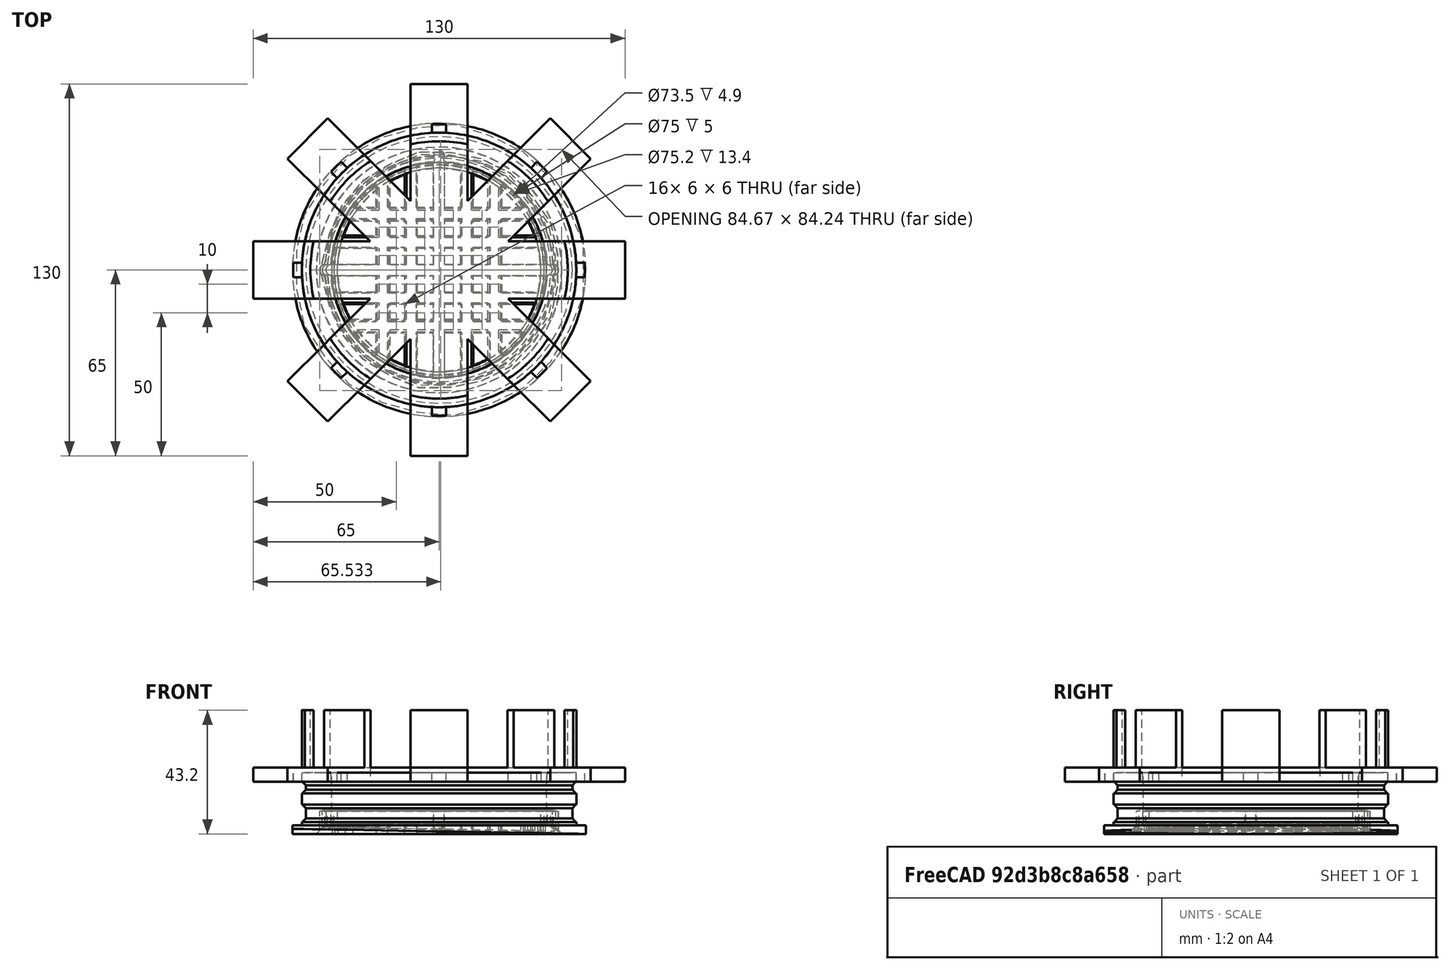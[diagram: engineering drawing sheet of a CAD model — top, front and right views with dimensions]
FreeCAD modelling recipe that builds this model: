
FCSTD DOCUMENT  (FreeCAD 0.18R4 (GitTag))
Label: rejilla_banio
License: CreativeCommons Attribution-ShareAlike
LicenseURL: http://creativecommons.org/licenses/by-sa/4.0/
objects: Part::Cylinder×56, Part::Cut×50, Part::Box×40, Part::MultiFuse×22, Part::FeaturePython×9, Part::Cone×3, Part::Plane×3, Part::Chamfer×2, App::DocumentObjectGroup×2, Part::Feature×2
note: 187 computed .brp shape members not serialized (recipe doc carries the construction recipe); baked Part::Feature solids carry a one-line shape summary decoded from their .brp

FEATURE [Part::Cone] Cone
  Angle = 360
  AttacherType = Attacher::AttachEngine3D
  Height = 5
  Placement = pos=(0,0,-15.2) rot=(0,1,0;3.14159rad)
  Radius1 = 40
  Radius2 = 45
FEATURE [Part::Cylinder] Cylinder007
  Angle = 360
  AttacherType = Attacher::AttachEngine3D
  Height = 25
  Placement = pos=(0,0,-23) rot=(0,0,1;0rad)
  Radius = 45
FEATURE [Part::Cylinder] Cylinder006  label="ajustar_radio_de_este"
  Angle = 360
  AttacherType = Attacher::AttachEngine3D
  Height = 5
  Placement = pos=(0,0,-20.2) rot=(0,0,1;0rad)
  Radius = 51.3
FEATURE [Part::Cut] Cut001
  Base = -> Cylinder006
  Tool = -> Cylinder007
FEATURE [Part::Cylinder] Cylinder001
  Angle = 360
  AttacherType = Attacher::AttachEngine3D
  Height = 4
  Placement = pos=(0,0,-4) rot=(0,0,1;0rad)
  Radius = 46.6
FEATURE [Part::Cylinder] Cylinder002
  Angle = 360
  AttacherType = Attacher::AttachEngine3D
  Height = 4
  Placement = pos=(0,0,-8) rot=(0,0,1;0rad)
  Radius = 48
FEATURE [Part::Cylinder] Cylinder003
  Angle = 360
  AttacherType = Attacher::AttachEngine3D
  Height = 6
  Placement = pos=(0,0,-14) rot=(0,0,1;0rad)
  Radius = 46.6
FEATURE [Part::Cylinder] Cylinder005
  Angle = 360
  AttacherType = Attacher::AttachEngine3D
  Height = 25
  Placement = pos=(0,0,-18) rot=(0,0,1;0rad)
  Radius = 45
FEATURE [Part::Cylinder] Cylinder008
  Angle = 360
  AttacherType = Attacher::AttachEngine3D
  Height = 23.4
  Placement = pos=(0,0,-20.2) rot=(0,0,1;0rad)
  Radius = 45
FEATURE [Part::Cylinder] Cylinder009
  Angle = 360
  AttacherType = Attacher::AttachEngine3D
  Height = 27.4
  Placement = pos=(0,0,-17) rot=(0,0,1;0rad)
  Radius = 40
FEATURE [Part::MultiFuse] Fusion002
  Shapes = -> [Cylinder009,Cone]
FEATURE [Part::Cut] Cut002
  Base = -> Cylinder008
  Tool = -> Fusion002
FEATURE [Part::Cylinder] Cylinder019  label="ajustar_radio_de_este001"
  Angle = 360
  AttacherType = Attacher::AttachEngine3D
  Height = 5
  Placement = pos=(0,0,-23.2) rot=(0,0,1;0rad)
  Radius = 68.3
FEATURE [Part::Cylinder] Cylinder
  Angle = 360
  AttacherType = Attacher::AttachEngine3D
  Height = 3.2
  Radius = 48
FEATURE [Part::Cylinder] Cylinder004
  Angle = 360
  AttacherType = Attacher::AttachEngine3D
  Height = 1.2
  Placement = pos=(0,0,-15.2) rot=(0,0,1;0rad)
  Radius = 48
FEATURE [Part::MultiFuse] Fusion
  Shapes = -> [Cylinder004,Cylinder,Cylinder003,Cylinder001,Cylinder002]
FEATURE [Part::Cut] Cut
  Base = -> Fusion
  Tool = -> Cylinder005
FEATURE [Part::MultiFuse] Fusion001
  Shapes = -> [Cut001,Cut]
FEATURE [Part::MultiFuse] Fusion003  label="rejilla_sin_cortar_oblicuo_sin_chaflan"
  Shapes = -> [Fusion001,Cut002]
FEATURE [Part::Chamfer] Chamfer
  Base = -> Fusion003
  Edges = 2 edges r=1.2: [Edge12,Edge24]
FEATURE [Part::Chamfer] Chamfer001  label="rejilla__exteriorsin_cortar_oblicuo_alta"
  Base = -> Chamfer
  Edges = 2 edges r=1.2: [Edge8,Edge26]
FEATURE [Part::Cut] Cut009  label="rejilla__exterior_sin_cortar_oblicuo_sin_muescas_01"
  Base = -> Chamfer001
  Tool = -> Cylinder019
FEATURE [Part::Cylinder] Cylinder057
  Angle = 360
  AttacherType = Attacher::AttachEngine3D
  Height = 7.8
  Placement = pos=(39.8,0,-18) rot=(0,0,1;0rad)
  Radius = 2
FEATURE [Part::Cylinder] Cylinder054
  Angle = 360
  AttacherType = Attacher::AttachEngine3D
  Height = 7.8
  Placement = pos=(0,39.8,-18) rot=(0,0,1;0rad)
  Radius = 2
FEATURE [Part::Cylinder] Cylinder058
  Angle = 360
  AttacherType = Attacher::AttachEngine3D
  Height = 7.8
  Placement = pos=(-39.8,0,-18) rot=(0,0,1;0rad)
  Radius = 2
FEATURE [Part::Cylinder] Cylinder055
  Angle = 360
  AttacherType = Attacher::AttachEngine3D
  Height = 13.4
  Placement = pos=(0,0,-10.2) rot=(0,0,1;0rad)
  Radius = 40
FEATURE [Part::Cylinder] Cylinder056
  Angle = 360
  AttacherType = Attacher::AttachEngine3D
  Height = 13.4
  Placement = pos=(0,0,-10.2) rot=(0,0,1;0rad)
  Radius = 37.6
FEATURE [Part::Cut] Cut026
  Base = -> Cylinder055
  Tool = -> Cylinder056
FEATURE [Part::MultiFuse] Fusion019  label="rejilla__exterior_sin_cortar_oblicuo_sin_muescas"
  Shapes = -> [Cut009,Cut026]
FEATURE [Part::Cut] Cut027
  Base = -> Fusion019
  Tool = -> Cylinder054
FEATURE [Part::Cut] Cut028
  Base = -> Cut027
  Tool = -> Cylinder057
FEATURE [Part::Cut] Cut029  label="rejilla__exterior_sin_cortar"
  Base = -> Cut028
  Tool = -> Cylinder058
FEATURE [Part::Cone] Cone003
  Angle = 360
  AttacherType = Attacher::AttachEngine3D
  Height = 5
  Placement = pos=(0,0,-15.2) rot=(0,1,0;3.14159rad)
  Radius1 = 39.85
  Radius2 = 44.9
FEATURE [Part::Box] Box015  label="Cube015"
  AttacherType = Attacher::AttachEngine3D
  Height = 5
  Length = 74
  Placement = pos=(-8,-37,-41) rot=(0,0,1;1.5708rad)
  Width = 4
FEATURE [Part::Cylinder] Cylinder046
  Angle = 360
  AttacherType = Attacher::AttachEngine3D
  Height = 5
  Placement = pos=(0,0,-41) rot=(0,0,1;0rad)
  Radius = 45
FEATURE [Part::Cylinder] Cylinder048
  Angle = 360
  AttacherType = Attacher::AttachEngine3D
  Height = 5
  Placement = pos=(0,0,-41) rot=(0,0,1;0rad)
  Radius = 37.5
FEATURE [Part::Box] Box016  label="Cube016"
  AttacherType = Attacher::AttachEngine3D
  Height = 5
  Length = 74
  Placement = pos=(-37,8,-41) rot=(0,0,1;0rad)
  Width = 4
FEATURE [Part::Box] Box017  label="Cube017"
  AttacherType = Attacher::AttachEngine3D
  Height = 5
  Length = 66
  Placement = pos=(-33,18,-41) rot=(0,0,1;0rad)
  Width = 4
FEATURE [Part::Cylinder] Cylinder042
  Angle = 360
  AttacherType = Attacher::AttachEngine3D
  Height = 5
  Radius = 37.5
FEATURE [Part::Cylinder] Cylinder043
  Angle = 360
  AttacherType = Attacher::AttachEngine3D
  Height = 5
  Radius = 39.9
FEATURE [Part::Cut] Cut021
  Base = -> Cylinder043
  Placement = pos=(0,0,-15.2) rot=(0,0,1;0rad)
  Tool = -> Cylinder042
FEATURE [Part::Box] Box010  label="Cube010"
  AttacherType = Attacher::AttachEngine3D
  Height = 5
  Length = 74
  Placement = pos=(12,-37,-41) rot=(0,0,1;1.5708rad)
  Width = 4
FEATURE [Part::Cylinder] Cylinder045
  Angle = 360
  AttacherType = Attacher::AttachEngine3D
  Height = 7.8
  Placement = pos=(-39.8,0,-18) rot=(0,0,1;0rad)
  Radius = 1.9
FEATURE [Part::Box] Box012  label="Cube012"
  AttacherType = Attacher::AttachEngine3D
  Height = 5
  Length = 66
  Placement = pos=(22,-33,-41) rot=(0,0,1;1.5708rad)
  Width = 4
FEATURE [Part::Cylinder] Cylinder047
  Angle = 360
  AttacherType = Attacher::AttachEngine3D
  Height = 7.8
  Placement = pos=(39.8,0,-18) rot=(0,0,1;0rad)
  Radius = 1.9
FEATURE [Part::Cylinder] Cylinder044
  Angle = 360
  AttacherType = Attacher::AttachEngine3D
  Height = 10
  Placement = pos=(0,0,-49) rot=(0,0,1;0rad)
  Radius = 50
FEATURE [Part::Box] Box013  label="Cube013"
  AttacherType = Attacher::AttachEngine3D
  Height = 5
  Length = 66
  Placement = pos=(-18,-33,-41) rot=(0,0,1;1.5708rad)
  Width = 4
FEATURE [Part::Box] Box014  label="Cube014"
  AttacherType = Attacher::AttachEngine3D
  Height = 5
  Length = 76
  Placement = pos=(-38,-2,-41) rot=(0,0,1;0rad)
  Width = 4
FEATURE [Part::Box] Box011  label="Cube011"
  AttacherType = Attacher::AttachEngine3D
  Height = 5
  Length = 66
  Placement = pos=(-33,-22,-41) rot=(0,0,1;0rad)
  Width = 4
FEATURE [Part::Cylinder] Cylinder050  label="ajustar_radio_de_este005"
  Angle = 360
  AttacherType = Attacher::AttachEngine3D
  Height = 5
  Placement = pos=(0,0,-23.2) rot=(0,0,1;0rad)
  Radius = 68.3
FEATURE [Part::Box] Box019  label="Cube019"
  AttacherType = Attacher::AttachEngine3D
  Height = 5
  Length = 76
  Placement = pos=(2,-38,-41) rot=(0,0,1;1.5708rad)
  Width = 4
FEATURE [Part::Cylinder] Cylinder052
  Angle = 360
  AttacherType = Attacher::AttachEngine3D
  Height = 5
  Placement = pos=(0,0,-41) rot=(0,0,1;0rad)
  Radius = 37.3
FEATURE [Part::Cut] Cut022  label="anillo001"
  Base = -> Cylinder048
  Tool = -> Cylinder052
FEATURE [Part::Cylinder] Cylinder051
  Angle = 360
  AttacherType = Attacher::AttachEngine3D
  Height = 32
  Placement = pos=(0,0,-39) rot=(0,0,1;0rad)
  Radius = 37.5
FEATURE [Part::Cut] Cut019
  Base = -> Cone003
  Tool = -> Cylinder051
FEATURE [Part::MultiFuse] Fusion015  label="rejilla_interior_sin_cortar_oblicuo_sin_tapa_006"
  Shapes = -> [Cut021,Cut019]
FEATURE [Part::Cut] Cut025
  Base = -> Fusion015
  Tool = -> Cylinder050
FEATURE [Part::Cylinder] Cylinder049
  Angle = 360
  AttacherType = Attacher::AttachEngine3D
  Height = 5
  Placement = pos=(0,0,-41) rot=(0,0,1;0rad)
  Radius = 37.5
FEATURE [Part::Cut] Cut020
  Base = -> Cylinder046
  Tool = -> Cylinder049
FEATURE [Part::Cylinder] Cylinder053
  Angle = 360
  AttacherType = Attacher::AttachEngine3D
  Height = 7.8
  Placement = pos=(0,39.8,-18) rot=(0,0,1;0rad)
  Radius = 1.9
FEATURE [Part::Box] Box018  label="Cube018"
  AttacherType = Attacher::AttachEngine3D
  Height = 5
  Length = 74
  Placement = pos=(-37,-12,-41) rot=(0,0,1;0rad)
  Width = 4
FEATURE [Part::MultiFuse] Fusion016
  Shapes = -> [Cut022,Box013,Box012,Box015,Box016,Box018,Box011,Box014,Box017,Box019,Box010]
FEATURE [Part::Cut] Cut023
  Base = -> Fusion016
  Tool = -> Cut020
FEATURE [Part::Cut] Cut024
  Base = -> Cut023
  Placement = pos=(0,0,20.8) rot=(0,0,1;0rad)
  Tool = -> Cylinder044
FEATURE [Part::MultiFuse] Fusion017  label="rejilla__interior_sin_cortar_oblicuo_sin_muescas001"
  Shapes = -> [Cut024,Cut025]
FEATURE [Part::MultiFuse] Fusion014  label="rejilla__interior_sin_cortar_oblicuo001"
  Shapes = -> [Fusion017,Cylinder045,Cylinder047]
FEATURE [Part::MultiFuse] Fusion018  label="rejilla__interior_v2.0_cono_39.85"
  Shapes = -> [Fusion014,Cylinder053]
FEATURE [Part::Plane] Plane
  AttacherType = Attacher::AttachEngine3D
  Length = 300
  Placement = pos=(-150,-150,-14.7) rot=(0,1,0;0.017453rad)
  Width = 300
FEATURE [Part::Plane] Plane001
  AttacherType = Attacher::AttachEngine3D
  Length = 300
  Placement = pos=(-150,-150,-14.7) rot=(0,1,0;0.017453rad)
  Width = 300
FEATURE [Part::FeaturePython] Slice  # WARN: FeaturePython — macro-defined, semantics opaque (R4)
  Base = -> Cut029
  Mode = 1
  Tolerance = 0
  Tools = -> [Plane001]
FEATURE [Part::FeaturePython] Slice_child0  label="rejilla_exterior"  # WARN: FeaturePython — macro-defined, semantics opaque (R4)
  Base = -> Slice
  FilterType = 1
  Invert = false
  OverrideMaxVal = 0
  WindowFrom = 80
  WindowTo = 100
  items = 0
FEATURE [Part::FeaturePython] Slice_child1  label="Slice.1"  # WARN: FeaturePython — macro-defined, semantics opaque (R4)
  Base = -> Slice
  FilterType = 1
  Invert = false
  OverrideMaxVal = 0
  WindowFrom = 80
  WindowTo = 100
  items = 1
FEATURE [App::DocumentObjectGroup] GrExplode_Slice  label="Exploded Slice"
  Group = -> [Slice_child0,Slice_child1]
FEATURE [Part::FeaturePython] Slice001  # WARN: FeaturePython — macro-defined, semantics opaque (R4)
  Base = -> Fusion018
  Mode = 1
  Tolerance = 0
  Tools = -> [Plane]
FEATURE [Part::FeaturePython] Slice001_child0  label="rejilla__interior"  # WARN: FeaturePython — macro-defined, semantics opaque (R4)
  Base = -> Slice001
  FilterType = 1
  Invert = false
  OverrideMaxVal = 0
  WindowFrom = 80
  WindowTo = 100
  items = 0
FEATURE [Part::FeaturePython] Slice001_child1  label="Slice001.1"  # WARN: FeaturePython — macro-defined, semantics opaque (R4)
  Base = -> Slice001
  FilterType = 1
  Invert = false
  OverrideMaxVal = 0
  WindowFrom = 80
  WindowTo = 100
  items = 1
FEATURE [App::DocumentObjectGroup] GrExplode_Slice001  label="Exploded Slice001"
  Group = -> [Slice001_child0,Slice001_child1]
FEATURE [Part::Feature] Slice001_child0001  label="rejilla__interior001"
  shape: bbox 85.47 x 85.49 x 7.864 mm, 285 faces (baked)
FEATURE [Part::Feature] Slice001_child  label="rejilla__interior_095"
  shape: bbox 151.1 x 139.8 x 7.471 mm, 285 faces (baked)
FEATURE [Part::Cylinder] Cylinder059
  Angle = 360
  AttacherType = Attacher::AttachEngine3D
  Height = 5
  Placement = pos=(0,0,-41) rot=(0,0,1;0rad)
  Radius = 45
FEATURE [Part::Box] Box020  label="Cube020"
  AttacherType = Attacher::AttachEngine3D
  Height = 5
  Length = 74
  Placement = pos=(-37,8,-41) rot=(0,0,1;0rad)
  Width = 4
FEATURE [Part::Box] Box021  label="Cube021"
  AttacherType = Attacher::AttachEngine3D
  Height = 5
  Length = 66
  Placement = pos=(-33,18,-41) rot=(0,0,1;0rad)
  Width = 4
FEATURE [Part::Box] Box022  label="Cube022"
  AttacherType = Attacher::AttachEngine3D
  Height = 5
  Length = 74
  Placement = pos=(-8,-37,-41) rot=(0,0,1;1.5708rad)
  Width = 4
FEATURE [Part::Cylinder] Cylinder060
  Angle = 360
  AttacherType = Attacher::AttachEngine3D
  Height = 5
  Placement = pos=(0,0,-41) rot=(0,0,1;0rad)
  Radius = 37.5
FEATURE [Part::Cone] Cone004
  Angle = 360
  AttacherType = Attacher::AttachEngine3D
  Height = 5
  Placement = pos=(0,0,-15.2) rot=(0,1,0;3.14159rad)
  Radius1 = 39.85
  Radius2 = 44.9
FEATURE [Part::Plane] Plane002
  AttacherType = Attacher::AttachEngine3D
  Length = 300
  Placement = pos=(-150,-150,-14.7) rot=(0,1,0;0.017453rad)
  Width = 300
FEATURE [Part::Cylinder] Cylinder061  label="ajustar_radio_de_este006"
  Angle = 360
  AttacherType = Attacher::AttachEngine3D
  Height = 5
  Placement = pos=(0,0,-23.2) rot=(0,0,1;0rad)
  Radius = 68.3
FEATURE [Part::Box] Box023  label="Cube023"
  AttacherType = Attacher::AttachEngine3D
  Height = 5
  Length = 74
  Placement = pos=(12,-37,-41) rot=(0,0,1;1.5708rad)
  Width = 4
FEATURE [Part::Box] Box024  label="Cube024"
  AttacherType = Attacher::AttachEngine3D
  Height = 5
  Length = 66
  Placement = pos=(-18,-33,-41) rot=(0,0,1;1.5708rad)
  Width = 4
FEATURE [Part::Cylinder] Cylinder062
  Angle = 360
  AttacherType = Attacher::AttachEngine3D
  Height = 7.8
  Placement = pos=(0,39.8,-18) rot=(0,0,1;0rad)
  Radius = 1.9
FEATURE [Part::Box] Box025  label="Cube025"
  AttacherType = Attacher::AttachEngine3D
  Height = 5
  Length = 74
  Placement = pos=(-37,-12,-41) rot=(0,0,1;0rad)
  Width = 4
FEATURE [Part::Cylinder] Cylinder063
  Angle = 360
  AttacherType = Attacher::AttachEngine3D
  Height = 10
  Placement = pos=(0,0,-49) rot=(0,0,1;0rad)
  Radius = 50
FEATURE [Part::Box] Box026  label="Cube026"
  AttacherType = Attacher::AttachEngine3D
  Height = 5
  Length = 76
  Placement = pos=(-38,-2,-41) rot=(0,0,1;0rad)
  Width = 4
FEATURE [Part::Cylinder] Cylinder064
  Angle = 360
  AttacherType = Attacher::AttachEngine3D
  Height = 5
  Radius = 37.5
FEATURE [Part::Cylinder] Cylinder065
  Angle = 360
  AttacherType = Attacher::AttachEngine3D
  Height = 5
  Placement = pos=(0,0,-41) rot=(0,0,1;0rad)
  Radius = 37.3
FEATURE [Part::Cut] Cut035  label="anillo002"
  Base = -> Cylinder060
  Tool = -> Cylinder065
FEATURE [Part::Box] Box027  label="Cube027"
  AttacherType = Attacher::AttachEngine3D
  Height = 5
  Length = 66
  Placement = pos=(-33,-22,-41) rot=(0,0,1;0rad)
  Width = 4
FEATURE [Part::Cylinder] Cylinder066
  Angle = 360
  AttacherType = Attacher::AttachEngine3D
  Height = 32
  Placement = pos=(0,0,-39) rot=(0,0,1;0rad)
  Radius = 37.5
FEATURE [Part::Cut] Cut030
  Base = -> Cone004
  Tool = -> Cylinder066
FEATURE [Part::Box] Box028  label="Cube028"
  AttacherType = Attacher::AttachEngine3D
  Height = 5
  Length = 66
  Placement = pos=(22,-33,-41) rot=(0,0,1;1.5708rad)
  Width = 4
FEATURE [Part::Box] Box029  label="Cube029"
  AttacherType = Attacher::AttachEngine3D
  Height = 5
  Length = 76
  Placement = pos=(2,-38,-41) rot=(0,0,1;1.5708rad)
  Width = 4
FEATURE [Part::MultiFuse] Fusion022
  Shapes = -> [Cut035,Box024,Box028,Box022,Box020,Box025,Box027,Box026,Box021,Box029,Box023]
FEATURE [Part::Cylinder] Cylinder067
  Angle = 360
  AttacherType = Attacher::AttachEngine3D
  Height = 5
  Placement = pos=(0,0,-41) rot=(0,0,1;0rad)
  Radius = 37.5
FEATURE [Part::Cut] Cut032
  Base = -> Cylinder059
  Tool = -> Cylinder067
FEATURE [Part::Cut] Cut036
  Base = -> Fusion022
  Tool = -> Cut032
FEATURE [Part::Cut] Cut034
  Base = -> Cut036
  Placement = pos=(0,0,20.8) rot=(0,0,1;0rad)
  Tool = -> Cylinder063
FEATURE [Part::Cylinder] Cylinder068
  Angle = 360
  AttacherType = Attacher::AttachEngine3D
  Height = 7.8
  Placement = pos=(-39.8,0,-18) rot=(0,0,1;0rad)
  Radius = 1.9
FEATURE [Part::Cylinder] Cylinder069
  Angle = 360
  AttacherType = Attacher::AttachEngine3D
  Height = 5
  Radius = 39.9
FEATURE [Part::Cut] Cut033
  Base = -> Cylinder069
  Placement = pos=(0,0,-15.2) rot=(0,0,1;0rad)
  Tool = -> Cylinder064
FEATURE [Part::MultiFuse] Fusion020  label="rejilla_interior_sin_cortar_oblicuo_sin_tapa_007"
  Shapes = -> [Cut033,Cut030]
FEATURE [Part::Cut] Cut031
  Base = -> Fusion020
  Tool = -> Cylinder061
FEATURE [Part::MultiFuse] Fusion023  label="rejilla__interior_sin_cortar_oblicuo_sin_muescas002"
  Shapes = -> [Cut034,Cut031]
FEATURE [Part::Cylinder] Cylinder070
  Angle = 360
  AttacherType = Attacher::AttachEngine3D
  Height = 7.8
  Placement = pos=(39.8,0,-18) rot=(0,0,1;0rad)
  Radius = 1.9
FEATURE [Part::MultiFuse] Fusion024  label="rejilla__interior_sin_cortar_oblicuo002"
  Shapes = -> [Fusion023,Cylinder068,Cylinder070]
FEATURE [Part::MultiFuse] Fusion021  label="rejilla__interior_v2.0_cono_39.086"
  Shapes = -> [Fusion024,Cylinder062]
FEATURE [Part::FeaturePython] Slice002  # WARN: FeaturePython — macro-defined, semantics opaque (R4)
  Base = -> Fusion021
  Mode = 1
  Tolerance = 0
  Tools = -> [Plane002]
FEATURE [Part::FeaturePython] Slice001_child0002  label="rejilla__interior100"  # WARN: FeaturePython — macro-defined, semantics opaque (R4)
  Base = -> Slice002
  FilterType = 1
  Invert = false
  OverrideMaxVal = 0
  WindowFrom = 80
  WindowTo = 100
  items = 0
FEATURE [Part::FeaturePython] Scale  label="rejilla_interior_8"  # Draft clone (typed FeaturePython)
  Fuse = false
  Objects = -> [Slice001_child0002]
  Scale = (0.98,0.98,0.98)
FEATURE [Part::Box] Box  label="Cube"
  AttacherType = Attacher::AttachEngine3D
  Height = 5
  Length = 130
  Placement = pos=(-65,-10,0) rot=(0,0,1;0rad)
  Width = 20
FEATURE [Part::Cylinder] Cylinder071
  Angle = 360
  AttacherType = Attacher::AttachEngine3D
  Height = 20
  Radius = 48
FEATURE [Part::Cylinder] Cylinder072
  Angle = 360
  AttacherType = Attacher::AttachEngine3D
  Height = 20
  Radius = 45
FEATURE [Part::Cut] Cut037
  Base = -> Cylinder071
  Placement = pos=(0,0,5) rot=(0,0,1;0rad)
  Tool = -> Cylinder072
FEATURE [Part::Cylinder] Cylinder073
  Angle = 360
  AttacherType = Attacher::AttachEngine3D
  Height = 10
  Radius = 48
FEATURE [Part::Cylinder] Cylinder074
  Angle = 360
  AttacherType = Attacher::AttachEngine3D
  Height = 10
  Radius = 51
FEATURE [Part::Cut] Cut038
  Base = -> Cylinder074
  Placement = pos=(0,0,-106) rot=(0,0,1;0rad)
  Tool = -> Cylinder073
FEATURE [Part::Box] Box030  label="Cube030"
  AttacherType = Attacher::AttachEngine3D
  Height = 20
  Length = 130
  Placement = pos=(-65,2.5,-108) rot=(0,0,1;0rad)
  Width = 60
FEATURE [Part::Box] Box031  label="Cube031"
  AttacherType = Attacher::AttachEngine3D
  Height = 20
  Length = 130
  Placement = pos=(-65,-62.5,-108) rot=(0,0,1;0rad)
  Width = 60
FEATURE [Part::Cut] Cut039
  Base = -> Cut038
  Tool = -> Box030
FEATURE [Part::Cut] Cut040
  Base = -> Cut039
  Placement = pos=(0,0,105) rot=(0,0,1;0rad)
  Tool = -> Box031
FEATURE [Part::Cut] Cut041
  Base = -> Box
  Tool = -> Cut040
FEATURE [Part::MultiFuse] Fusion025
  Shapes = -> [Cut041,Cut037]
FEATURE [Part::Box] Box032  label="Cube032"
  AttacherType = Attacher::AttachEngine3D
  Height = 30
  Length = 130
  Placement = pos=(-65,10,0) rot=(0,0,1;0rad)
  Width = 50
FEATURE [Part::Box] Box033  label="Cube033"
  AttacherType = Attacher::AttachEngine3D
  Height = 30
  Length = 130
  Placement = pos=(-65,-60,0) rot=(0,0,1;0rad)
  Width = 50
FEATURE [Part::Cut] Cut042
  Base = -> Fusion025
  Tool = -> Box032
FEATURE [Part::Cut] Cut043
  Base = -> Cut042
  Tool = -> Box033
FEATURE [Part::Box] Box034  label="Cube034"
  AttacherType = Attacher::AttachEngine3D
  Height = 5
  Length = 130
  Placement = pos=(-65,-10,0) rot=(0,0,1;0rad)
  Width = 20
FEATURE [Part::Cylinder] Cylinder075
  Angle = 360
  AttacherType = Attacher::AttachEngine3D
  Height = 10
  Radius = 51
FEATURE [Part::Box] Box035  label="Cube035"
  AttacherType = Attacher::AttachEngine3D
  Height = 30
  Length = 130
  Placement = pos=(-65,10,0) rot=(0,0,1;0rad)
  Width = 50
FEATURE [Part::Cylinder] Cylinder076
  Angle = 360
  AttacherType = Attacher::AttachEngine3D
  Height = 10
  Radius = 48
FEATURE [Part::Box] Box036  label="Cube036"
  AttacherType = Attacher::AttachEngine3D
  Height = 20
  Length = 130
  Placement = pos=(-65,-62.5,-108) rot=(0,0,1;0rad)
  Width = 60
FEATURE [Part::Cylinder] Cylinder077
  Angle = 360
  AttacherType = Attacher::AttachEngine3D
  Height = 20
  Radius = 48
FEATURE [Part::Cylinder] Cylinder078
  Angle = 360
  AttacherType = Attacher::AttachEngine3D
  Height = 20
  Radius = 45
FEATURE [Part::Box] Box037  label="Cube037"
  AttacherType = Attacher::AttachEngine3D
  Height = 30
  Length = 130
  Placement = pos=(-65,-60,0) rot=(0,0,1;0rad)
  Width = 50
FEATURE [Part::Box] Box038  label="Cube038"
  AttacherType = Attacher::AttachEngine3D
  Height = 20
  Length = 130
  Placement = pos=(-65,2.5,-108) rot=(0,0,1;0rad)
  Width = 60
FEATURE [Part::Cut] Cut044
  Base = -> Cylinder077
  Placement = pos=(0,0,5) rot=(0,0,1;0rad)
  Tool = -> Cylinder078
FEATURE [Part::Cut] Cut048
  Base = -> Cylinder075
  Placement = pos=(0,0,-106) rot=(0,0,1;0rad)
  Tool = -> Cylinder076
FEATURE [Part::Cut] Cut045
  Base = -> Cut048
  Tool = -> Box038
FEATURE [Part::Cut] Cut046
  Base = -> Cut045
  Placement = pos=(0,0,105) rot=(0,0,1;0rad)
  Tool = -> Box036
FEATURE [Part::Cut] Cut047
  Base = -> Box034
  Tool = -> Cut046
FEATURE [Part::MultiFuse] Fusion026
  Shapes = -> [Cut047,Cut044]
FEATURE [Part::Cut] Cut050
  Base = -> Fusion026
  Tool = -> Box035
FEATURE [Part::Cut] Cut049
  Base = -> Cut050
  Placement = pos=(0,0,0) rot=(0,0,1;-1.5708rad)
  Tool = -> Box037
FEATURE [Part::MultiFuse] Fusion027
  Shapes = -> [Cut043,Cut049]
FEATURE [Part::Box] Box039  label="Cube039"
  AttacherType = Attacher::AttachEngine3D
  Height = 30
  Length = 130
  Placement = pos=(-65,-60,0) rot=(0,0,1;0rad)
  Width = 50
FEATURE [Part::Box] Box040  label="Cube040"
  AttacherType = Attacher::AttachEngine3D
  Height = 5
  Length = 130
  Placement = pos=(-65,-10,0) rot=(0,0,1;0rad)
  Width = 20
FEATURE [Part::Cylinder] Cylinder079
  Angle = 360
  AttacherType = Attacher::AttachEngine3D
  Height = 10
  Radius = 51
FEATURE [Part::Box] Box041  label="Cube041"
  AttacherType = Attacher::AttachEngine3D
  Height = 30
  Length = 130
  Placement = pos=(-65,10,0) rot=(0,0,1;0rad)
  Width = 50
FEATURE [Part::Cylinder] Cylinder080
  Angle = 360
  AttacherType = Attacher::AttachEngine3D
  Height = 10
  Radius = 48
FEATURE [Part::Box] Box042  label="Cube042"
  AttacherType = Attacher::AttachEngine3D
  Height = 20
  Length = 130
  Placement = pos=(-65,-62.5,-108) rot=(0,0,1;0rad)
  Width = 60
FEATURE [Part::Cylinder] Cylinder081
  Angle = 360
  AttacherType = Attacher::AttachEngine3D
  Height = 20
  Radius = 48
FEATURE [Part::Cylinder] Cylinder082
  Angle = 360
  AttacherType = Attacher::AttachEngine3D
  Height = 10
  Radius = 51
FEATURE [Part::Cylinder] Cylinder083
  Angle = 360
  AttacherType = Attacher::AttachEngine3D
  Height = 20
  Radius = 45
FEATURE [Part::Cylinder] Cylinder084
  Angle = 360
  AttacherType = Attacher::AttachEngine3D
  Height = 10
  Radius = 48
FEATURE [Part::Box] Box043  label="Cube043"
  AttacherType = Attacher::AttachEngine3D
  Height = 20
  Length = 130
  Placement = pos=(-65,-62.5,-108) rot=(0,0,1;0rad)
  Width = 60
FEATURE [Part::Cylinder] Cylinder085
  Angle = 360
  AttacherType = Attacher::AttachEngine3D
  Height = 20
  Radius = 48
FEATURE [Part::Cylinder] Cylinder086
  Angle = 360
  AttacherType = Attacher::AttachEngine3D
  Height = 20
  Radius = 45
FEATURE [Part::Box] Box044  label="Cube044"
  AttacherType = Attacher::AttachEngine3D
  Height = 30
  Length = 130
  Placement = pos=(-65,-60,0) rot=(0,0,1;0rad)
  Width = 50
FEATURE [Part::Box] Box045  label="Cube045"
  AttacherType = Attacher::AttachEngine3D
  Height = 5
  Length = 130
  Placement = pos=(-65,-10,0) rot=(0,0,1;0rad)
  Width = 20
FEATURE [Part::Box] Box046  label="Cube046"
  AttacherType = Attacher::AttachEngine3D
  Height = 30
  Length = 130
  Placement = pos=(-65,10,0) rot=(0,0,1;0rad)
  Width = 50
FEATURE [Part::Box] Box047  label="Cube047"
  AttacherType = Attacher::AttachEngine3D
  Height = 20
  Length = 130
  Placement = pos=(-65,2.5,-108) rot=(0,0,1;0rad)
  Width = 60
FEATURE [Part::Cut] Cut051
  Base = -> Cylinder081
  Placement = pos=(0,0,5) rot=(0,0,1;0rad)
  Tool = -> Cylinder083
FEATURE [Part::Cut] Cut055
  Base = -> Cylinder082
  Placement = pos=(0,0,-106) rot=(0,0,1;0rad)
  Tool = -> Cylinder080
FEATURE [Part::Cut] Cut058
  Base = -> Cylinder085
  Placement = pos=(0,0,5) rot=(0,0,1;0rad)
  Tool = -> Cylinder086
FEATURE [Part::Cut] Cut062
  Base = -> Cylinder079
  Placement = pos=(0,0,-106) rot=(0,0,1;0rad)
  Tool = -> Cylinder084
FEATURE [Part::Cut] Cut059
  Base = -> Cut062
  Tool = -> Box047
FEATURE [Part::Cut] Cut060
  Base = -> Cut059
  Placement = pos=(0,0,105) rot=(0,0,1;0rad)
  Tool = -> Box043
FEATURE [Part::Cut] Cut061
  Base = -> Box040
  Tool = -> Cut060
FEATURE [Part::MultiFuse] Fusion028
  Shapes = -> [Cut061,Cut058]
FEATURE [Part::Cut] Cut064
  Base = -> Fusion028
  Tool = -> Box041
FEATURE [Part::Cut] Cut063
  Base = -> Cut064
  Tool = -> Box044
FEATURE [Part::Box] Box048  label="Cube048"
  AttacherType = Attacher::AttachEngine3D
  Height = 20
  Length = 130
  Placement = pos=(-65,2.5,-108) rot=(0,0,1;0rad)
  Width = 60
FEATURE [Part::Cut] Cut053
  Base = -> Cut055
  Tool = -> Box048
FEATURE [Part::Cut] Cut052
  Base = -> Cut053
  Placement = pos=(0,0,105) rot=(0,0,1;0rad)
  Tool = -> Box042
FEATURE [Part::Cut] Cut054
  Base = -> Box045
  Tool = -> Cut052
FEATURE [Part::MultiFuse] Fusion029
  Shapes = -> [Cut054,Cut051]
FEATURE [Part::Cut] Cut057
  Base = -> Fusion029
  Tool = -> Box046
FEATURE [Part::Cut] Cut056
  Base = -> Cut057
  Placement = pos=(0,0,0) rot=(0,0,-1;1.5708rad)
  Tool = -> Box039
FEATURE [Part::MultiFuse] Fusion030
  Placement = pos=(0,0,0) rot=(0,0,1;0.785398rad)
  Shapes = -> [Cut063,Cut056]
FEATURE [Part::MultiFuse] Fusion031  label="medidor"
  Shapes = -> [Fusion030,Fusion027]
